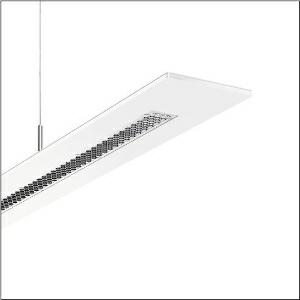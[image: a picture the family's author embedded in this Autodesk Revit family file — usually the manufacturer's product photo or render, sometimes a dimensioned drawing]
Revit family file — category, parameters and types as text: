
# Revit family: arktika_r__21_5mb251dl30840_e160
name_source: partatom
category: Lighting Fixtures
units: mm (PartAtom-declared; Revit-internal decimal feet)

## family parameters
Cut with Voids When Loaded = No
Host = Face
Light Source = No
Part Type = Normal
Room Calculation Point = No
Round Connector Dimension = Use Diameter
Shared = No

## types (1)
- --- (1 x LED 4000K / CRI = 80 (unbekannt), 4400 lm, 4000K)
    Apparent Load = 34 VA
    CIE Flux Codes = 81 100 100 79 100
    Color Rendering = 80
    Color Temperature = 4000K
    Default Elevation = 1800 mm
    Description = Arktika® 21, office luminaire, primary anti-glare with honeycomb louvre, of plastic, aluminium vaporised, highly specular, light emission: direct/indirect distribution, primary light characteristic: symmetric, installation type: suspended mounting, LED rated luminous flux: 4.400 lm, light colour: 840, colour temperature: 4000K, control gear: ECG DALI, with terminal, 3+2-pole, max. 2.5mm², mains connection: 220..240V, AC, 50/60Hz, rated input power: 34W, housing, of aluminium, powder-coated, traffic white (RAL 9016), 1-length, length: 1.250 mm, width: 120 mm, height: 8mm, protection rating (complete): IP20, insulation class (complete): insulation class II (safety insulation), certification: CE, ENEC, VDE, packaging unit: 1 piece
    Height = 8 mm  [stored 0.0262467 ft]
    Lamp = 1 x LED 4000K / CRI >= 80 (unbekannt)
    Lamp Light Flux = 4400 lm
    Lamp count = 1
    Length = 1250 mm
    Luminous efficacy = 131 lm/W
    Manufacturer = Siteco
    ModVariant = No
    Model = 5MB251DL30840
    Mounting Place = Ceiling
    Mounting Type = Pendant
    Number of Poles = 1
    OnlyDefault = Yes
    Power Factor = 1
    Product Name = Arktika® 21
    Product group = office luminaire | ceiling pendant
    ProductGroupID = 905
    Protection Class = Protection class II
    Protection Degree = IP 20
    RLX_Detail_Level = 1
    RlxData = <blob elided: 39169 chars, md5=371021dc>
    Socket = socket
    Standby Power = 0 W
    System Light Flux = 4400 lm
    System Power = 34 W
    Type Comments = factory setting: luminous flux: 100 % | dim-lin: 254 | 665 mA
    Type Image = l_1006128.jpg
    URL = http://relux.com
    VarID = @adj_145873
    Voltage = 0 V
    Weight = 0.00 kg
    Width = 120 mm

note: [stored X ft] marks values corroborated as IEEE doubles in the binary element streams (Revit-internal decimal feet)

## geometry (parser evidence)
native form markers: Blend x4, Sweep x12
no freeform markers — native parametric forms only
